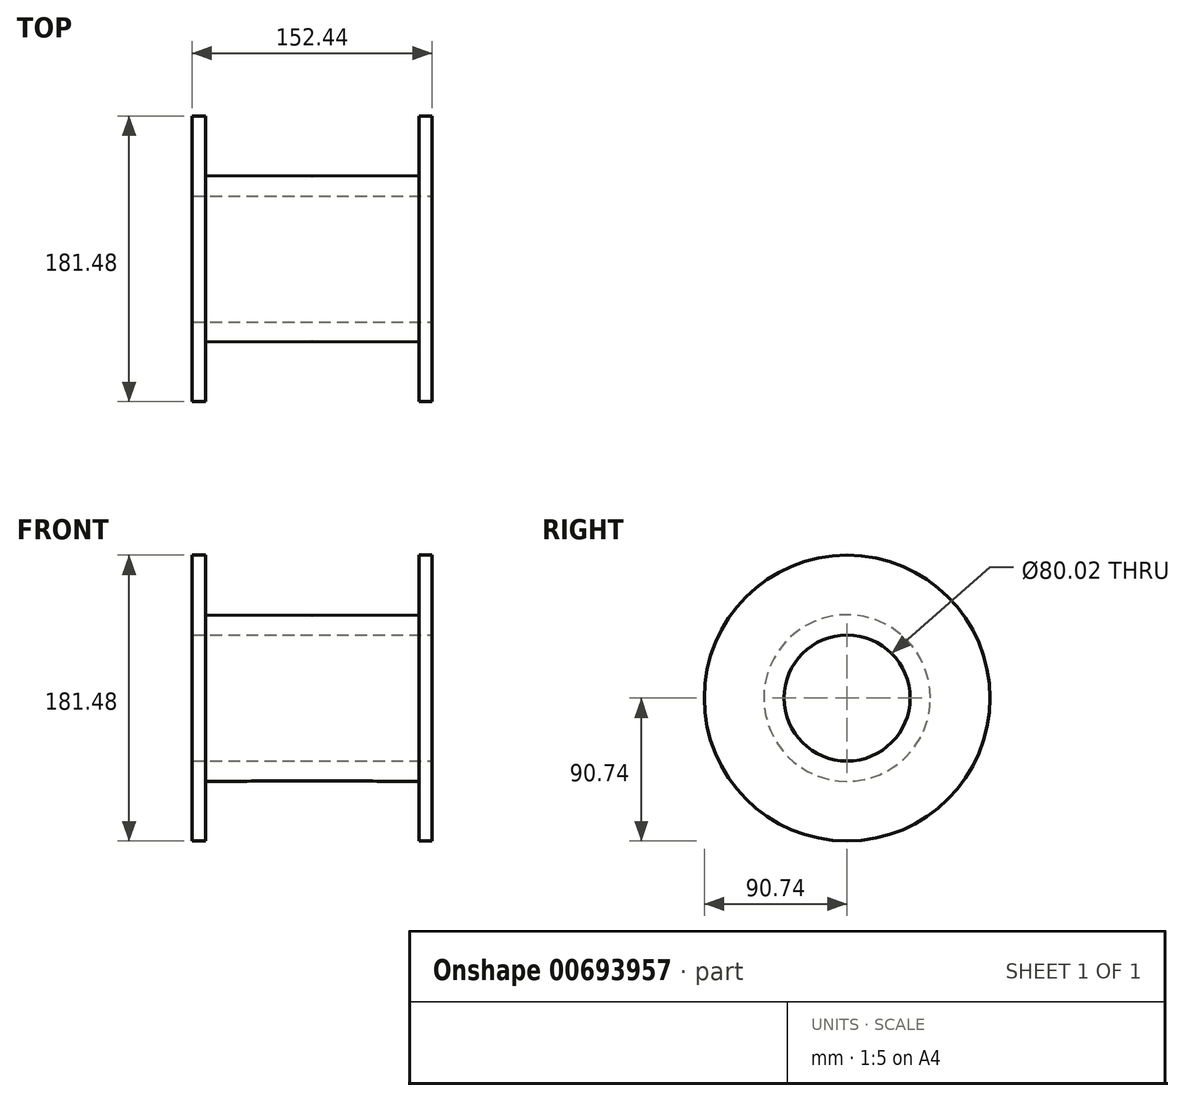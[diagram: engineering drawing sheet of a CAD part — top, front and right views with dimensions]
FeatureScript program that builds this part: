
annotation { "Feature Type Name" : "Feature", "Feature Type Description" : "" }
export const myFeature = defineFeature(function(context is Context, id is Id, definition is map)
    precondition{}
    {
        {
            var Q0;
            Q0=qCreatedBy(makeId("Front.planeOp"),FACE);
            var sketch = newSketch(context, id + "F0", { "sketchPlane" : qUnion([Q0])});
            skLineSegment(sketch, "E0", {"start": v(0, 0) * mm, "end": v(-79.95, 0) * mm, "construction": true});
            skLineSegment(sketch, "E1", {"start": v(0, 52.62) * mm, "end": v(0, 40) * mm});
            skLineSegment(sketch, "E2", {"start": v(0, 40) * mm, "end": v(-76.22, 40) * mm});
            skLineSegment(sketch, "E3", {"start": v(-76.22, 40) * mm, "end": v(-76.22, 90.74) * mm});
            skLineSegment(sketch, "E4", {"start": v(-76.22, 90.74) * mm, "end": v(-67.81, 90.74) * mm});
            skLineSegment(sketch, "E5", {"start": v(-67.81, 90.74) * mm, "end": v(-67.81, 52.9) * mm});
            skLineSegment(sketch, "E6", {"start": v(-67.81, 52.9) * mm, "end": v(0, 52.62) * mm});
            skLineSegment(sketch, "E7.MirrorCS", {"start": v(67.81, 52.9) * mm, "end": v(0, 52.62) * mm});
            skLineSegment(sketch, "E8.MirrorCS", {"start": v(67.81, 90.74) * mm, "end": v(67.81, 52.9) * mm});
            skLineSegment(sketch, "E9.MirrorCS", {"start": v(76.22, 40) * mm, "end": v(76.22, 90.74) * mm});
            skLineSegment(sketch, "E10.MirrorCS", {"start": v(76.22, 90.74) * mm, "end": v(67.81, 90.74) * mm});
            skLineSegment(sketch, "E11.MirrorCS", {"start": v(0, 40) * mm, "end": v(76.22, 40) * mm});
            skSolve(sketch);
        }
        {
            var Q0;
            Q0=makeQuery(id+"F0.imprint","IMPRINT",FACE,{"disambiguationData":[TD([[makeQuery(id+"F0.imprint","IMPRINT",EDGE,{"derivedFrom":sQuery(id+"F0.wireOp",EDGE,"E2")}),-1.0]])]});
            var Q1;
            Q1=makeQuery(id+"F0.imprint","IMPRINT",FACE,{"disambiguationData":[TD([[makeQuery(id+"F0.imprint","IMPRINT",EDGE,{"derivedFrom":sQuery(id+"F0.wireOp",EDGE,"E7.MirrorCS")}),1.0]])]});
            var Q2;
            Q2=sQuery(id+"F0.wireOp",EDGE,"E0");
            revolve(context, id + "F1", {"entities" : qUnion([Q0, Q1]), "axis" : qUnion([Q2]), "revolveType" : RevolveType.FULL});
        }
    });
